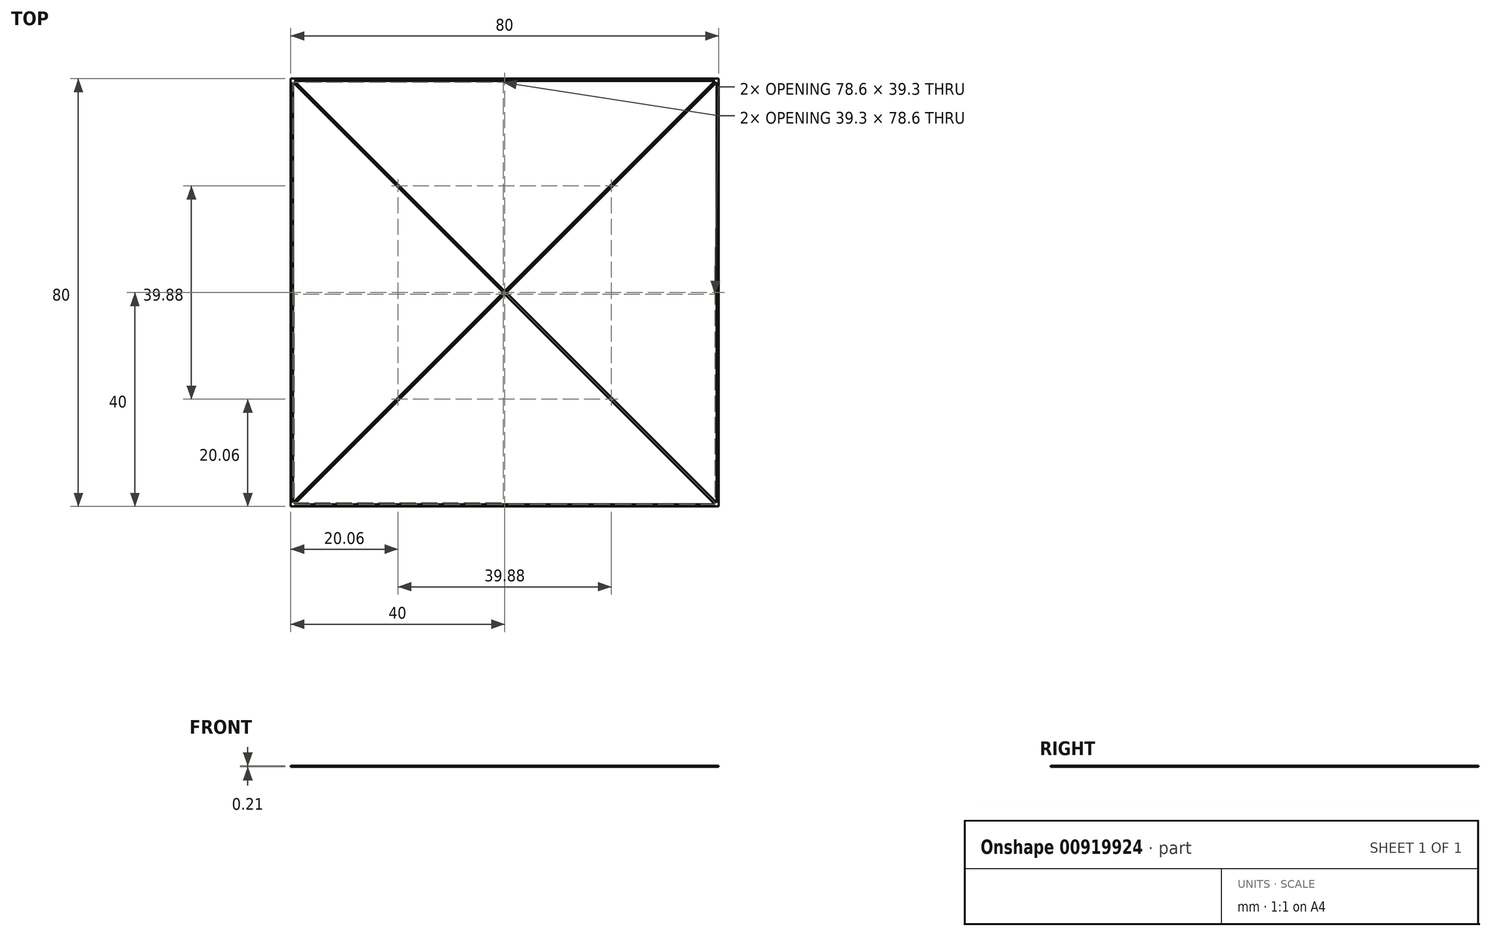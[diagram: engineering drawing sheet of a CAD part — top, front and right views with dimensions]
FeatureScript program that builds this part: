
annotation { "Feature Type Name" : "Feature", "Feature Type Description" : "" }
export const myFeature = defineFeature(function(context is Context, id is Id, definition is map)
    precondition{}
    {
        {
            assignVariable(context, id + "F0", {"name" : "lineDepth", "anyValue" : 0.2});
        }
        {
            var Q0;
            Q0=qCreatedBy(makeId("Top.planeOp"),FACE);
            var sketch = newSketch(context, id + "F1", { "sketchPlane" : qUnion([Q0])});
            skLineSegment(sketch, "E0.bottom", {"start": v(40, -40) * mm, "end": v(-40, -40) * mm});
            skLineSegment(sketch, "E0.top", {"start": v(40, 40) * mm, "end": v(-40, 40) * mm});
            skLineSegment(sketch, "E0.left", {"start": v(40, -40) * mm, "end": v(40, 40) * mm});
            skLineSegment(sketch, "E0.right", {"start": v(-40, -40) * mm, "end": v(-40, 40) * mm});
            skPoint(sketch, "E0.middle", {"position": v(0, 0) * mm});
            skLineSegment(sketch, "E1.bottom", {"start": v(39.6, -39.6) * mm, "end": v(-39.6, -39.6) * mm});
            skLineSegment(sketch, "E1.top", {"start": v(39.6, 39.6) * mm, "end": v(-39.6, 39.6) * mm});
            skLineSegment(sketch, "E1.left", {"start": v(39.6, -39.6) * mm, "end": v(39.6, 39.6) * mm});
            skLineSegment(sketch, "E1.right", {"start": v(-39.6, -39.6) * mm, "end": v(-39.6, 39.6) * mm});
            skLineSegment(sketch, "E2", {"start": v(0, 39.6) * mm, "end": v(0, 40) * mm});
            skLineSegment(sketch, "E3", {"start": v(-39.6, 0) * mm, "end": v(-40, 0) * mm});
            skLineSegment(sketch, "E4", {"start": v(-39.6, 39.6) * mm, "end": v(39.6, -39.6) * mm});
            skLineSegment(sketch, "E5.0", {"start": v(-39.66, 39.94) * mm, "end": v(39.94, -39.66) * mm});
            skLineSegment(sketch, "E6.0", {"start": v(-39.94, 39.66) * mm, "end": v(39.66, -39.94) * mm});
            skLineSegment(sketch, "E7.MirrorCS", {"start": v(39.94, 39.66) * mm, "end": v(-39.66, -39.94) * mm});
            skLineSegment(sketch, "E8.MirrorCS", {"start": v(39.6, 39.6) * mm, "end": v(-39.6, -39.6) * mm});
            skLineSegment(sketch, "E9.MirrorCS", {"start": v(39.66, 39.94) * mm, "end": v(-39.94, -39.66) * mm});
            skSolve(sketch);
        }
        {
            var Q0;
            {var subQ4=sQuery(id+"F1.wireOp",EDGE,"E2");Q0=makeQuery(id+"F1.imprint","IMPRINT",FACE,{"disambiguationData":[TD([[makeQuery(id+"F1.imprint","IMPRINT",EDGE,{"derivedFrom":subQ4}),1.0]])]});}
            var Q1;
            {var subQ1=sQuery(id+"F1.wireOp",EDGE,"E0.bottom");Q1=makeQuery(id+"F1.imprint","IMPRINT",FACE,{"disambiguationData":[TD([[makeQuery(id+"F1.imprint","IMPRINT",EDGE,{"derivedFrom":subQ1}),-1.0]])]});}
            var Q2;
            {var subQ1=sQuery(id+"F1.wireOp",EDGE,"E1.right");var subQ3=sQuery(id+"F1.wireOp",EDGE,"E6.0");var subQ4=makeQuery(id+"F1.imprint","INTERSECT",VERTEX,{"derivedFrom":[subQ1,subQ3]});Q2=makeQuery(id+"F1.imprint","IMPRINT",FACE,{"disambiguationData":[TD([[makeQuery(id+"F1.imprint","IMPRINT",EDGE,{"disambiguationData":[TD([[subQ4,-1.0]])],"derivedFrom":subQ3}),1.0]])]});}
            var Q3;
            {var subQ1=sQuery(id+"F1.wireOp",EDGE,"E1.top");var subQ3=sQuery(id+"F1.wireOp",EDGE,"E5.0");var subQ4=makeQuery(id+"F1.imprint","INTERSECT",VERTEX,{"derivedFrom":[subQ1,subQ3]});Q3=makeQuery(id+"F1.imprint","IMPRINT",FACE,{"disambiguationData":[TD([[makeQuery(id+"F1.imprint","IMPRINT",EDGE,{"disambiguationData":[TD([[subQ4,-1.0]])],"derivedFrom":subQ3}),-1.0]])]});}
            var Q4;
            {var subQ3=sQuery(id+"F1.wireOp",EDGE,"E9.MirrorCS");var subQ5=sQuery(id+"F1.wireOp",EDGE,"E5.0");var subQ6=makeQuery(id+"F1.imprint","INTERSECT",VERTEX,{"derivedFrom":[subQ5,subQ3]});Q4=makeQuery(id+"F1.imprint","IMPRINT",FACE,{"disambiguationData":[TD([[makeQuery(id+"F1.imprint","IMPRINT",EDGE,{"disambiguationData":[TD([[subQ6,-1.0]])],"derivedFrom":subQ5}),1.0]])]});}
            var Q5;
            {var subQ0=sQuery(id+"F1.wireOp",EDGE,"E8.MirrorCS");var subQ5=sQuery(id+"F1.wireOp",EDGE,"E5.0");var subQ6=makeQuery(id+"F1.imprint","INTERSECT",VERTEX,{"derivedFrom":[subQ5,subQ0]});Q5=makeQuery(id+"F1.imprint","IMPRINT",FACE,{"disambiguationData":[TD([[makeQuery(id+"F1.imprint","IMPRINT",EDGE,{"disambiguationData":[TD([[subQ6,-1.0]])],"derivedFrom":subQ5}),1.0]])]});}
            var Q6;
            {var subQ0=sQuery(id+"F1.wireOp",EDGE,"E8.MirrorCS");var subQ1=sQuery(id+"F1.wireOp",EDGE,"E4");var subQ2=makeQuery(id+"F1.imprint","INTERSECT",VERTEX,{"derivedFrom":[subQ1,subQ0]});Q6=makeQuery(id+"F1.imprint","IMPRINT",FACE,{"disambiguationData":[TD([[makeQuery(id+"F1.imprint","IMPRINT",EDGE,{"disambiguationData":[TD([[subQ2,-1.0]])],"derivedFrom":subQ1}),1.0]])]});}
            var Q7;
            {var subQ0=sQuery(id+"F1.wireOp",EDGE,"E9.MirrorCS");var subQ1=sQuery(id+"F1.wireOp",EDGE,"E4");var subQ2=makeQuery(id+"F1.imprint","INTERSECT",VERTEX,{"derivedFrom":[subQ1,subQ0]});Q7=makeQuery(id+"F1.imprint","IMPRINT",FACE,{"disambiguationData":[TD([[makeQuery(id+"F1.imprint","IMPRINT",EDGE,{"disambiguationData":[TD([[subQ2,-1.0]])],"derivedFrom":subQ1}),1.0]])]});}
            var Q8;
            {var subQ0=sQuery(id+"F1.wireOp",EDGE,"E9.MirrorCS");var subQ1=sQuery(id+"F1.wireOp",EDGE,"E4");var subQ2=makeQuery(id+"F1.imprint","INTERSECT",VERTEX,{"derivedFrom":[subQ1,subQ0]});Q8=makeQuery(id+"F1.imprint","IMPRINT",FACE,{"disambiguationData":[TD([[makeQuery(id+"F1.imprint","IMPRINT",EDGE,{"disambiguationData":[TD([[subQ2,-1.0]])],"derivedFrom":subQ1}),-1.0]])]});}
            var Q9;
            {var subQ0=sQuery(id+"F1.wireOp",EDGE,"E8.MirrorCS");var subQ1=sQuery(id+"F1.wireOp",EDGE,"E4");var subQ2=makeQuery(id+"F1.imprint","INTERSECT",VERTEX,{"derivedFrom":[subQ1,subQ0]});Q9=makeQuery(id+"F1.imprint","IMPRINT",FACE,{"disambiguationData":[TD([[makeQuery(id+"F1.imprint","IMPRINT",EDGE,{"disambiguationData":[TD([[subQ2,-1.0]])],"derivedFrom":subQ1}),-1.0]])]});}
            var Q10;
            {var subQ1=sQuery(id+"F1.wireOp",EDGE,"E1.bottom");var subQ3=sQuery(id+"F1.wireOp",EDGE,"E6.0");var subQ4=makeQuery(id+"F1.imprint","INTERSECT",VERTEX,{"derivedFrom":[subQ1,subQ3]});Q10=makeQuery(id+"F1.imprint","IMPRINT",FACE,{"disambiguationData":[TD([[makeQuery(id+"F1.imprint","IMPRINT",EDGE,{"disambiguationData":[TD([[subQ4,1.0]])],"derivedFrom":subQ3}),1.0]])]});}
            var Q11;
            {var subQ1=sQuery(id+"F1.wireOp",EDGE,"E1.left");var subQ3=sQuery(id+"F1.wireOp",EDGE,"E5.0");var subQ4=makeQuery(id+"F1.imprint","INTERSECT",VERTEX,{"derivedFrom":[subQ1,subQ3]});Q11=makeQuery(id+"F1.imprint","IMPRINT",FACE,{"disambiguationData":[TD([[makeQuery(id+"F1.imprint","IMPRINT",EDGE,{"disambiguationData":[TD([[subQ4,1.0]])],"derivedFrom":subQ3}),-1.0]])]});}
            var Q12;
            {var subQ0=sQuery(id+"F1.wireOp",EDGE,"E8.MirrorCS");var subQ5=sQuery(id+"F1.wireOp",EDGE,"E6.0");var subQ6=makeQuery(id+"F1.imprint","INTERSECT",VERTEX,{"derivedFrom":[subQ5,subQ0]});Q12=makeQuery(id+"F1.imprint","IMPRINT",FACE,{"disambiguationData":[TD([[makeQuery(id+"F1.imprint","IMPRINT",EDGE,{"disambiguationData":[TD([[subQ6,-1.0]])],"derivedFrom":subQ5}),-1.0]])]});}
            var Q13;
            {var subQ3=sQuery(id+"F1.wireOp",EDGE,"E9.MirrorCS");var subQ5=sQuery(id+"F1.wireOp",EDGE,"E6.0");var subQ6=makeQuery(id+"F1.imprint","INTERSECT",VERTEX,{"derivedFrom":[subQ5,subQ3]});Q13=makeQuery(id+"F1.imprint","IMPRINT",FACE,{"disambiguationData":[TD([[makeQuery(id+"F1.imprint","IMPRINT",EDGE,{"disambiguationData":[TD([[subQ6,-1.0]])],"derivedFrom":subQ5}),-1.0]])]});}
            extrude(context, id + "F2", {"entities" : qUnion([Q0, Q1, Q2, Q3, Q4, Q5, Q6, Q7, Q8, Q9, Q10, Q11, Q12, Q13]), "depth" : (getVariable(context, 'lineDepth')) * mm, "offsetDistance" : 25 * mm});
        }
    });
